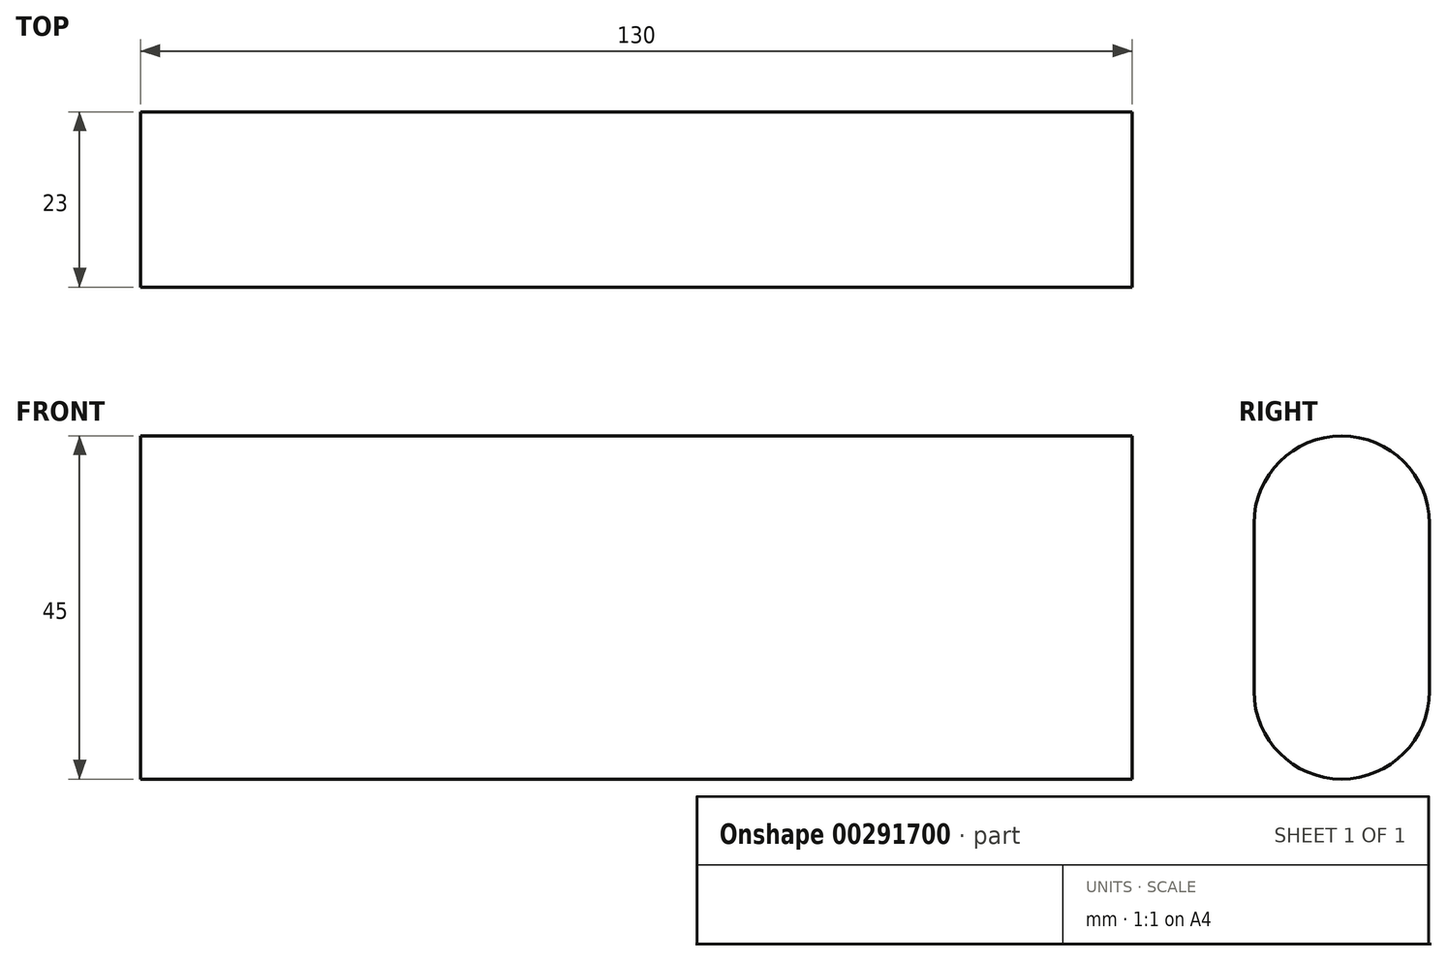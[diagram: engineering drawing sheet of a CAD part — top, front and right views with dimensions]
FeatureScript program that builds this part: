
annotation { "Feature Type Name" : "Feature", "Feature Type Description" : "" }
export const myFeature = defineFeature(function(context is Context, id is Id, definition is map)
    precondition{}
    {
        {
            var Q0;
            Q0=qCreatedBy(makeId("Right.planeOp"),FACE);
            var sketch = newSketch(context, id + "F0", { "sketchPlane" : qUnion([Q0])});
            skLineSegment(sketch, "E0", {"start": v(0, 11) * mm, "end": v(0, -11) * mm, "construction": true});
            skLineSegment(sketch, "E1", {"start": v(-11.5, 11) * mm, "end": v(-11.5, -11) * mm});
            skLineSegment(sketch, "E2", {"start": v(11.5, 11) * mm, "end": v(11.5, -11) * mm});
            skArc(sketch, "E3", {"start": v(11.5, 11) * mm, "mid": v(0, 22.5) * mm, "end": v(-11.5, 11) * mm});
            skArc(sketch, "E4", {"start": v(-11.5, -11) * mm, "mid": v(0, -22.5) * mm, "end": v(11.5, -11) * mm});
            skLineSegment(sketch, "E5", {"start": v(-11.5, -11) * mm, "end": v(11.5, -11) * mm, "construction": true});
            skSolve(sketch);
        }
        {
            var Q0;
            Q0=qSketchRegion(id+"F0",true);
            extrude(context, id + "F1", {"entities" : qUnion([Q0]), "depth" : 130 * mm});
        }
    });
